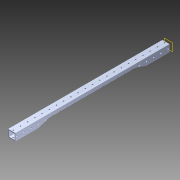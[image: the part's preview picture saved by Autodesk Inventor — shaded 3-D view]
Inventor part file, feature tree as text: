
AUTODESK INVENTOR PART (.ipt)
format: ipt  version: 2014 (Build 180170000, 170)  size: 1,309,184 bytes
history: native  units: in
note: dims shown in document units (in); Inventor stores cm internally (conversion verified against a paired STEP export)
features: extrude x3, sketch x3, pattern_circular x1, other x1, plane x1, imported_body x1, projected_geometry x1
ambient origin geometry x8: Origin, YZ Plane, XZ Plane, XY Plane, X Axis, Y Axis, Z Axis, Center Point
bodies: Body1 (feature_tree)
feature tree (11):
  pattern_circular  "CirPattern2"
  other  "217-3426-STEP1"
  plane  "Work Plane1"
  extrude  "Extrusion1"  Depth=3937.0079in TaperAngle=0.0deg
  extrude  "Extrusion2"  Depth=21.375in
  extrude  "Extrusion3"  Depth=1.0in TaperAngle=0.0deg
  imported_body  "Base1"
  sketch  "Sketch1"  dims[d0=-22.0in d1=3937.0079in d2=0.0in]
  sketch  "Sketch3"  dims[d3=21.375in d4=11.0in]
  projected_geometry  "Projected Loop1"
  sketch  "Sketch4"  dims[d5=2.0in d6=0.0in d7=1.0in d8=0.0in d9=1.5in d10=1.5in]
